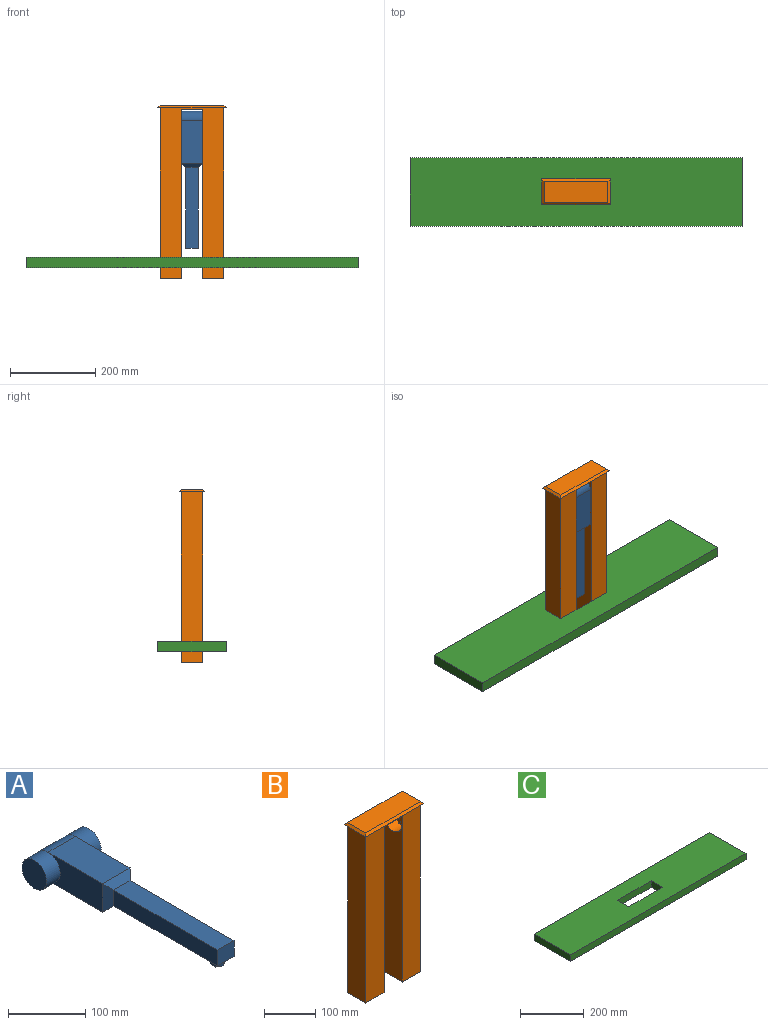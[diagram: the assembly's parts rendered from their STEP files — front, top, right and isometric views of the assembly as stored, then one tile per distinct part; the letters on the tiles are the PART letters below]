
ASSEMBLY  parts=3 mates=2
PART A: 32 faces, bbox 100x322.5x45 mm
  f0: cylinder r=22.4mm len=44.8mm, axis (-1,0,0), area 3518.6mm2, adj f6,f31
  f1: cylinder r=22.4mm len=44.8mm, axis (1,0,0), area 3518.6mm2, adj f5,f30
  f2: plane 100x50mm, normal (0,0,1), area 5000mm2, adj f3,f5,f6,f13
  f3: cylinder r=22.5mm len=50mm, axis (1,0,0), area 3534.3mm2, adj f2,f4,f5,f6
  f4: plane 100x50mm, normal (0,0,-1), area 5000mm2, adj f3,f5,f6,f14
  f5: plane 122.5x45mm, normal (-1,0,0), area 3718.9mm2, adj f1,f2,f3,f4,f15
  f6: plane 122.5x45mm, normal (1,0,0), area 3718.9mm2, adj f0,f2,f3,f4,f12
  f7: plane 190x30mm, normal (0,0,-1), area 5440.2mm2, adj f8,f10,f11,f14,f16,f17,f18,f19
  f8: plane 190x25mm, normal (1,0,0), area 4750mm2, adj f7,f9,f11,f12
  f9: plane 190x30mm, normal (0,0,1), area 5700mm2, adj f8,f10,f11,f13
  f10: plane 190x25mm, normal (-1,0,0), area 4750mm2, adj f7,f9,f11,f15
  f11: plane 30x25mm, normal (0,-1,0), area 750mm2, adj f7,f8,f9,f10
  f12: plane 45x10mm, normal (0.71,-0.71,0), area 495mm2, adj f6,f8,f13,f14
  f13: plane 50x10mm, normal (0,-0.71,0.71), area 565.7mm2, adj f2,f9,f12,f15
  f14: plane 50x10mm, normal (0,-0.71,-0.71), area 565.7mm2, adj f4,f7,f12,f15
  f15: plane 45x10mm, normal (-0.71,-0.71,0), area 495mm2, adj f5,f10,f13,f14
  f16: plane 10x8.66mm, normal (0.5,-0.87,0), area 100mm2, adj f7,f17,f21,f22
  f17: plane 10x8.66mm, normal (-0.5,-0.87,0), area 100mm2, adj f7,f16,f18,f22
  f18: plane 10x10mm, normal (-1,0,0), area 100mm2, adj f7,f17,f19,f22
  f19: plane 10x8.66mm, normal (-0.5,0.87,0), area 100mm2, adj f7,f18,f20,f22
  f20: plane 10x8.66mm, normal (0.5,0.87,0), area 100mm2, adj f7,f19,f21,f22
  f21: plane 10x10mm, normal (1,0,0), area 100mm2, adj f7,f16,f20,f22
  f22: plane 20x17.32mm, normal (0,0,-1), area 106.1mm2, adj f16,f17,f18,f19,f20,f21,f23,f24
  f23: plane 30x7.69mm, normal (-1,0,0), area 230.7mm2, adj f22,f24,f28,f29
  f24: plane 30x6.66mm, normal (-0.5,0.87,0), area 230.7mm2, adj f22,f23,f25,f29
  f25: plane 30x6.66mm, normal (0.5,0.87,0), area 230.7mm2, adj f22,f24,f26,f29
  f26: plane 30x7.69mm, normal (1,0,0), area 230.7mm2, adj f22,f25,f27,f29
  f27: plane 30x6.66mm, normal (0.5,-0.87,0), area 230.7mm2, adj f22,f26,f28,f29
  f28: plane 30x6.66mm, normal (-0.5,-0.87,0), area 230.7mm2, adj f22,f23,f27,f29
  f29: plane 15.38x13.32mm, normal (0,0,-1), area 153.7mm2, adj f23,f24,f25,f26,f27,f28
  f30: plane 44.8x44.8mm, normal (-1,0,0), area 1576.3mm2, adj f1
  f31: plane 44.8x44.8mm, normal (1,0,0), area 1576.3mm2, adj f0
PART B: 19 faces, bbox 160x60x405 mm
  f0: plane 395x50mm, normal (-1,0,0), area 18159.6mm2, adj f2,f4,f8,f9,f18
  f1: plane 395x50mm, normal (1,0,0), area 18159.6mm2, adj f2,f4,f5,f8,f17
  f2: plane 400x150mm, normal (0,1,0), area 40250mm2, adj f0,f1,f3,f7,f8,f11,f17,f18
  f3: plane 400x50mm, normal (-1,0,0), area 20000mm2, adj f2,f4,f11,f17
  f4: plane 400x150mm, normal (0,-1,0), area 40250mm2, adj f0,f1,f3,f7,f8,f11,f17,f18
  f5: cylinder r=22.5mm len=45mm, axis (1,0,0), area 3534.3mm2, adj f1,f6
  f6: plane 45x45mm, normal (1,0,0), area 1590.4mm2, adj f5
  f7: plane 400x50mm, normal (1,0,0), area 20000mm2, adj f2,f4,f11,f18
  f8: plane 50x50mm, normal (0,0,-1), area 2500mm2, adj f0,f1,f2,f4
  f9: cylinder r=22.5mm len=45mm, axis (-1,0,0), area 3534.3mm2, adj f0,f10
  f10: plane 45x45mm, normal (-1,0,0), area 1590.4mm2, adj f9
  f11: plane 160x60mm, normal (0,0,-1), area 2100mm2, adj f2,f3,f4,f7,f13,f14,f15,f16
  f12: plane 150x50mm, normal (0,0,1), area 7500mm2, adj f13,f14,f15,f16
  f13: plane 160x5mm, normal (0,0.71,0.71), area 1096mm2, adj f11,f12,f14,f15
  f14: plane 60x5mm, normal (-0.71,0,0.71), area 388.9mm2, adj f11,f12,f13,f16
  f15: plane 60x5mm, normal (0.71,0,0.71), area 388.9mm2, adj f11,f12,f13,f16
  f16: plane 160x5mm, normal (0,-0.71,0.71), area 1096mm2, adj f11,f12,f14,f15
  f17: plane 50x50mm, normal (0,0,-1), area 2500mm2, adj f1,f2,f3,f4
  f18: plane 50x50mm, normal (0,0,-1), area 2500mm2, adj f0,f2,f4,f7
PART C: 10 faces, bbox 778.9x160.3x25 mm
  f0: plane 160.27x25mm, normal (1,0,0), area 4006.8mm2, adj f1,f7,f8,f9
  f1: plane 778.88x25mm, normal (0,1,0), area 19472.1mm2, adj f0,f2,f8,f9
  f2: plane 160.27x25mm, normal (-1,0,0), area 4006.8mm2, adj f1,f7,f8,f9
  f3: plane 50x25mm, normal (1,0,0), area 1250mm2, adj f4,f6,f8,f9
  f4: plane 150x25mm, normal (0,-1,0), area 3750mm2, adj f3,f5,f8,f9
  f5: plane 50x25mm, normal (-1,0,0), area 1250mm2, adj f4,f6,f8,f9
  f6: plane 150x25mm, normal (0,1,0), area 3750mm2, adj f3,f5,f8,f9
  f7: plane 778.88x25mm, normal (0,-1,0), area 19472.1mm2, adj f0,f2,f8,f9
  f8: plane 778.88x160.27mm, normal (0,0,-1), area 117332.7mm2, adj f0,f1,f2,f3,f4,f5,f6,f7
  f9: plane 778.88x160.27mm, normal (0,0,1), area 117332.7mm2, adj f0,f1,f2,f3,f4,f5,f6,f7
PLACE A rot(axis=(1,0,0),90deg) t=(-200.89,-237.13,1191.22)mm
PLACE B t=(-200.89,-512.13,839.22)mm
PLACE C t=(-200.89,-721.13,794.22)mm
MATE revolute A.f0 <-> B.f5  axis (-1,0,0) through (-250.89,-512.13,1114.22)mm
MATE slider B.f11 <-> C.f9  axis (0,0,-1) through (-125.89,-537.13,1144.22)mm
